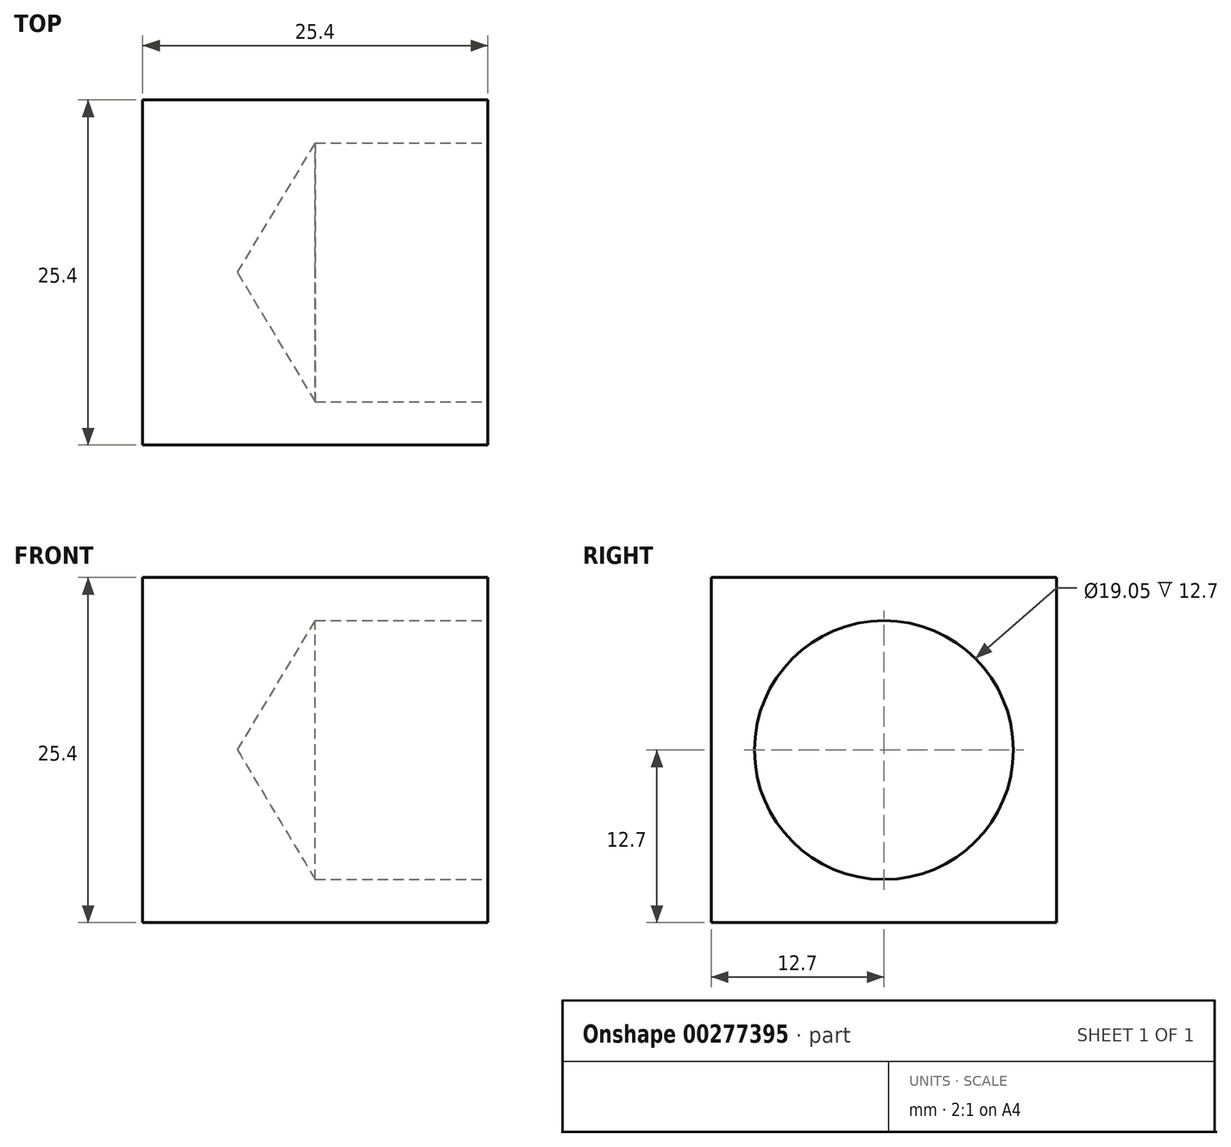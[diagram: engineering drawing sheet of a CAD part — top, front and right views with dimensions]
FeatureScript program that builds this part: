
annotation { "Feature Type Name" : "Feature", "Feature Type Description" : "" }
export const myFeature = defineFeature(function(context is Context, id is Id, definition is map)
    precondition{}
    {
        {
            var Q0;
            Q0=qCreatedBy(makeId("Right.planeOp"),FACE);
            var sketch = newSketch(context, id + "F0", { "sketchPlane" : qUnion([Q0])});
            skLineSegment(sketch, "E0.bottom", {"start": v(0, 0) * mm, "end": v(-25.4, 0) * mm});
            skLineSegment(sketch, "E0.top", {"start": v(0, 25.4) * mm, "end": v(-25.4, 25.4) * mm});
            skLineSegment(sketch, "E0.left", {"start": v(0, 0) * mm, "end": v(0, 25.4) * mm});
            skLineSegment(sketch, "E0.right", {"start": v(-25.4, 0) * mm, "end": v(-25.4, 25.4) * mm});
            skSolve(sketch);
        }
        {
            var Q0;
            Q0 = qSketchRegion(id + "F0", true);
            extrude(context, id + "F1", {"entities" : qUnion([Q0]), "depth" : 25.4 * mm});
        }
        {
            var Q0;
            Q0=makeQuery(id+"F1.opExtrude","CAP_FACE",FACE,{"disambiguationData":[OSD([sQuery(id+"F0.wireOp",EDGE,"E0.bottom"),sQuery(id+"F0.wireOp",EDGE,"E0.top"),sQuery(id+"F0.wireOp",EDGE,"E0.left"),sQuery(id+"F0.wireOp",EDGE,"E0.right")])],"isStart":false});
            var sketch = newSketch(context, id + "F2", { "sketchPlane" : qUnion([Q0])});
            skLineSegment(sketch, "E1", {"start": v(-25.4, 25.4) * mm, "end": v(0, 0) * mm});
            skLineSegment(sketch, "E2", {"start": v(0, 25.4) * mm, "end": v(-25.4, 0) * mm});
            skPoint(sketch, "E3", {"position": v(-12.7, 12.7) * mm});
            skSolve(sketch);
        }
        {
            var Q0;
            Q0=sQuery(id+"F2.wireOp",VERTEX,"E3");
            var Q1;
            Q1=makeQuery(id+"F1.opExtrude","SWEPT_BODY",BODY,{"disambiguationData":[OSD([sQuery(id+"F0.wireOp",EDGE,"E0.bottom"),sQuery(id+"F0.wireOp",EDGE,"E0.top"),sQuery(id+"F0.wireOp",EDGE,"E0.left"),sQuery(id+"F0.wireOp",EDGE,"E0.right")])]});
            hole(context, id + "F3", {"style" : HoleStyle.SIMPLE, "endStyle" : HoleEndStyle.BLIND, "holeDiameter" : 19.05 * mm, "holeDepth" : 12.7 * mm, "isTappedThrough" : true, "tappedDepth" : 12.7 * mm, "tapClearance" : 3, "locations" : qUnion([Q0]), "scope" : qUnion([Q1])});
        }
    });
